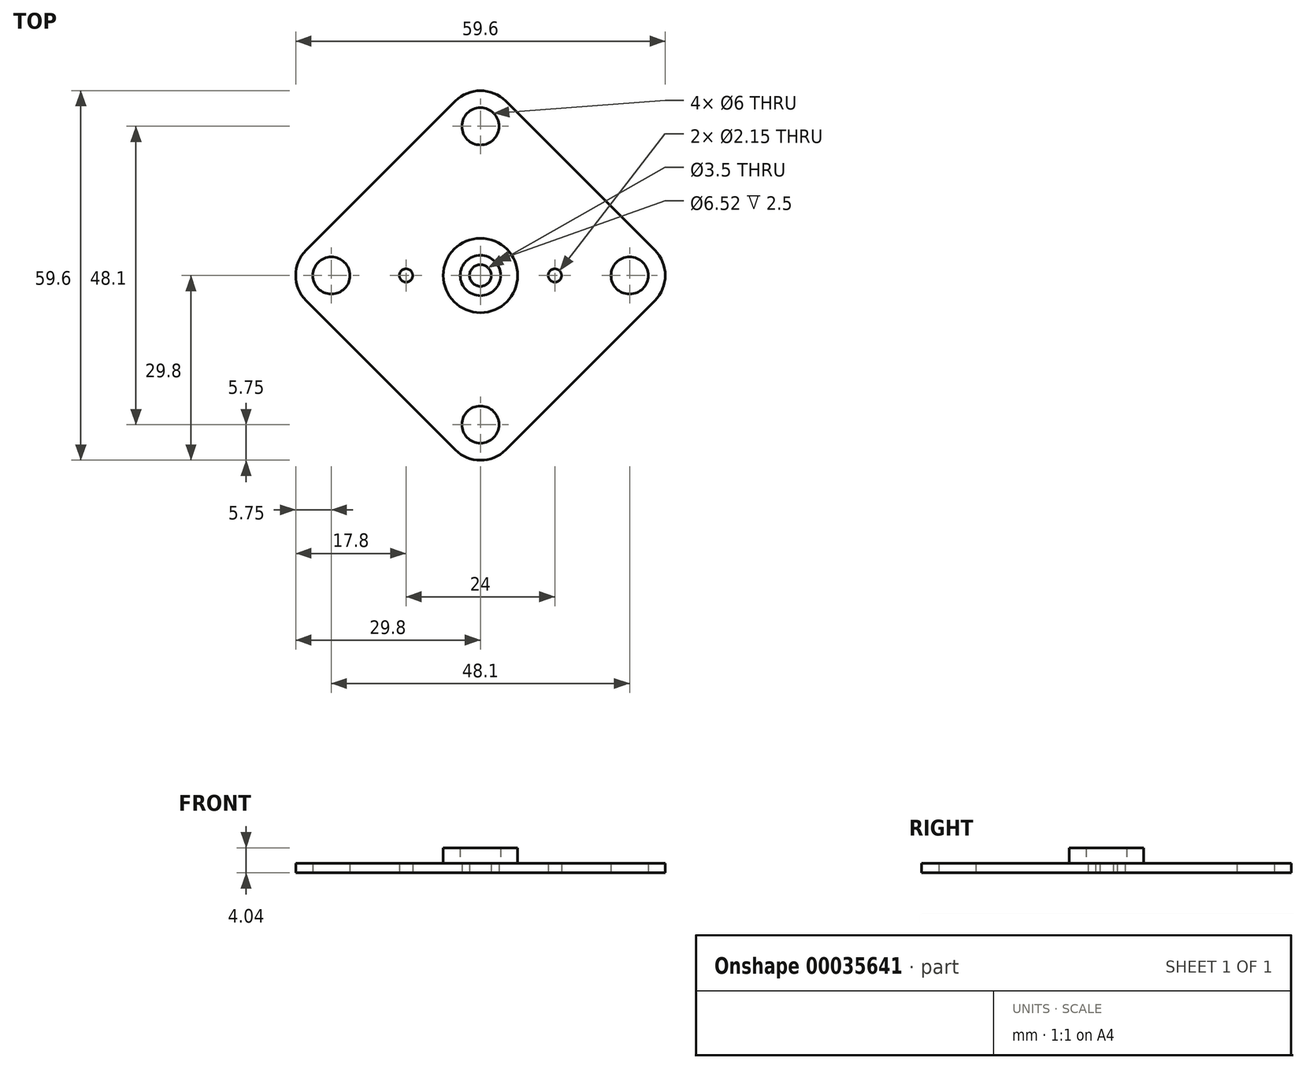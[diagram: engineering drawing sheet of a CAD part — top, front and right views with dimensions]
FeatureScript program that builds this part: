
annotation { "Feature Type Name" : "Feature", "Feature Type Description" : "" }
export const myFeature = defineFeature(function(context is Context, id is Id, definition is map)
    precondition{}
    {
        {
            var Q0;
            Q0=qCreatedBy(makeId("Top.planeOp"),FACE);
            var sketch = newSketch(context, id + "F0", { "sketchPlane" : qUnion([Q0])});
            skLineSegment(sketch, "E0", {"start": v(0, 24.05) * mm, "end": v(0, -24.05) * mm, "construction": true});
            skLineSegment(sketch, "E1", {"start": v(-29.8, 0) * mm, "end": v(29.8, 0) * mm, "construction": true});
            skPoint(sketch, "E2.center", {"position": v(0, 0) * mm});
            skArc(sketch, "E3", {"start": v(4.07, 28.12) * mm, "mid": v(0, 29.8) * mm, "end": v(-4.07, 28.12) * mm});
            skCircle(sketch, "E4", {"center": v(0, 24.05) * mm, "radius": 3 * mm});
            skPoint(sketch, "E5", {"position": v(-24.05, 0) * mm});
            skPoint(sketch, "E6", {"position": v(24.05, 0) * mm});
            skCircle(sketch, "E7", {"center": v(-24.05, 0) * mm, "radius": 3 * mm});
            skCircle(sketch, "E8", {"center": v(0, -24.05) * mm, "radius": 3 * mm});
            skCircle(sketch, "E9", {"center": v(24.05, 0) * mm, "radius": 3 * mm});
            skArc(sketch, "E10", {"start": v(-28.12, 4.07) * mm, "mid": v(-29.8, 0) * mm, "end": v(-28.12, -4.07) * mm});
            skArc(sketch, "E11", {"start": v(28.12, -4.07) * mm, "mid": v(29.8, 0) * mm, "end": v(28.12, 4.07) * mm});
            skArc(sketch, "E12", {"start": v(-4.07, -28.12) * mm, "mid": v(0, -29.8) * mm, "end": v(4.07, -28.12) * mm});
            skLineSegment(sketch, "E13", {"start": v(-28.12, -4.07) * mm, "end": v(-4.07, -28.12) * mm});
            skLineSegment(sketch, "E14", {"start": v(-4.07, 28.12) * mm, "end": v(-28.12, 4.07) * mm});
            skLineSegment(sketch, "E15", {"start": v(28.12, 4.07) * mm, "end": v(4.07, 28.12) * mm});
            skLineSegment(sketch, "E16", {"start": v(28.12, -4.07) * mm, "end": v(4.07, -28.12) * mm});
            skCircle(sketch, "E17", {"center": v(0, 0) * mm, "radius": 1.75 * mm});
            skLineSegment(sketch, "E18", {"start": v(0, -23.9) * mm, "end": v(0, -43.55) * mm, "construction": true});
            skCircle(sketch, "E19", {"center": v(-12, 0) * mm, "radius": 1.07 * mm});
            skCircle(sketch, "E20.MirrorC", {"center": v(12, 0) * mm, "radius": 1.07 * mm});
            skLineSegment(sketch, "E21", {"start": v(-12, -4.07) * mm, "end": v(-12, 4.07) * mm, "construction": true});
            skSolve(sketch);
        }
        {
            var Q0;
            Q0=makeQuery(id+"F0.imprint","IMPRINT",FACE,{"disambiguationData":[TD([[makeQuery(id+"F0.imprint","IMPRINT",EDGE,{"derivedFrom":sQuery(id+"F0.wireOp",EDGE,"E3")}),1.0]])]});
            extrude(context, id + "F1", {"entities" : qUnion([Q0]), "depth" : 1.54 * mm});
        }
        {
            var Q0;
            Q0=makeQuery(id+"F1.opExtrude","CAP_FACE",FACE,{"disambiguationData":[OSD([sQuery(id+"F0.wireOp",EDGE,"E3"),sQuery(id+"F0.wireOp",EDGE,"E4"),sQuery(id+"F0.wireOp",EDGE,"E7"),sQuery(id+"F0.wireOp",EDGE,"E8"),sQuery(id+"F0.wireOp",EDGE,"E9"),sQuery(id+"F0.wireOp",EDGE,"E10"),sQuery(id+"F0.wireOp",EDGE,"E11"),sQuery(id+"F0.wireOp",EDGE,"E12"),sQuery(id+"F0.wireOp",EDGE,"E13"),sQuery(id+"F0.wireOp",EDGE,"E14"),sQuery(id+"F0.wireOp",EDGE,"E15"),sQuery(id+"F0.wireOp",EDGE,"E16"),sQuery(id+"F0.wireOp",EDGE,"E17"),sQuery(id+"F0.wireOp",EDGE,"E19"),sQuery(id+"F0.wireOp",EDGE,"E20.MirrorC")])],"isStart":false});
            var sketch = newSketch(context, id + "F2", { "sketchPlane" : qUnion([Q0])});
            skCircle(sketch, "E22", {"center": v(0, 0) * mm, "radius": 3.26 * mm});
            skCircle(sketch, "E23", {"center": v(0, 0) * mm, "radius": 6 * mm});
            skSolve(sketch);
        }
        {
            var Q0;
            Q0 = qSketchRegion(id + "F2", true);
            extrude(context, id + "F3", {"entities" : qUnion([Q0]), "operationType" : NewBodyOperationType.ADD, "depth" : 2.5 * mm});
        }
    });
